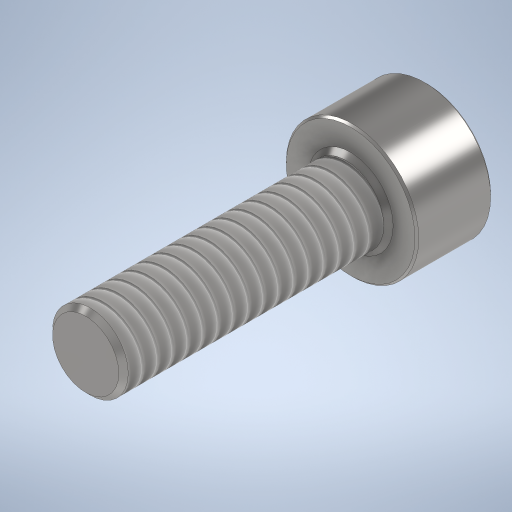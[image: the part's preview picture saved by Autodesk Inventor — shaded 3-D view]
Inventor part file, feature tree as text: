
AUTODESK INVENTOR PART (.ipt)
format: ipt  version: 2024 (Build 280153000, 153)  size: 330,752 bytes
history: native  units: mm
features: extrude x3, chamfer x3, sketch x2, thread x1, hole x1
ambient origin geometry x8: Origin, YZ Plane, XZ Plane, XY Plane, X Axis, Y Axis, Z Axis, Center Point
bodies: Solid1 (feature_tree)
feature tree (10):
  sketch  "Sketch1"  dims[d0=7.0mm d1=4.0mm]
  extrude  "Extrusion1"  Depth=4.0mm
  extrude  "Extrusion2"  Depth=2.0mm TaperAngle=0.0deg
  thread  "Thread1"  [1 undecoded]
  chamfer  "Chamfer1"  Distance=2.0mm Angle=45.0deg
  sketch  "Sketch2"  dims[d2=14.0mm d3=0.0mm d4=4.0mm d5=0.0mm d6=15.0mm d7=0.0mm d8=0.1mm d9=2.0mm d10=45.0deg d11=2.75mm d12=3.0mm d15=0.4mm d16=2.0mm d17=45.0deg d18=3.0mm d19=0.0mm d20=0.25mm d21=2.0mm d22=45.0deg d23=2.75mm d24=6.0mm d25=4.0mm d26=2.0mm d27=90.0deg d28=2.0mm d29=150.0deg]
  hole  "Hole1"  [1 undecoded]
  chamfer  "Chamfer2"  Distance=3.0mm
  extrude  "Extrusion4"  Depth=2.0mm TaperAngle=45.0deg
  chamfer  "Chamfer3"  Distance=3.0mm
note: 2 required parameter values undecoded (feature->parameter linkage not recoverable at this tier; creation-order binding heuristic only, values carry confidence <= 0.55)
